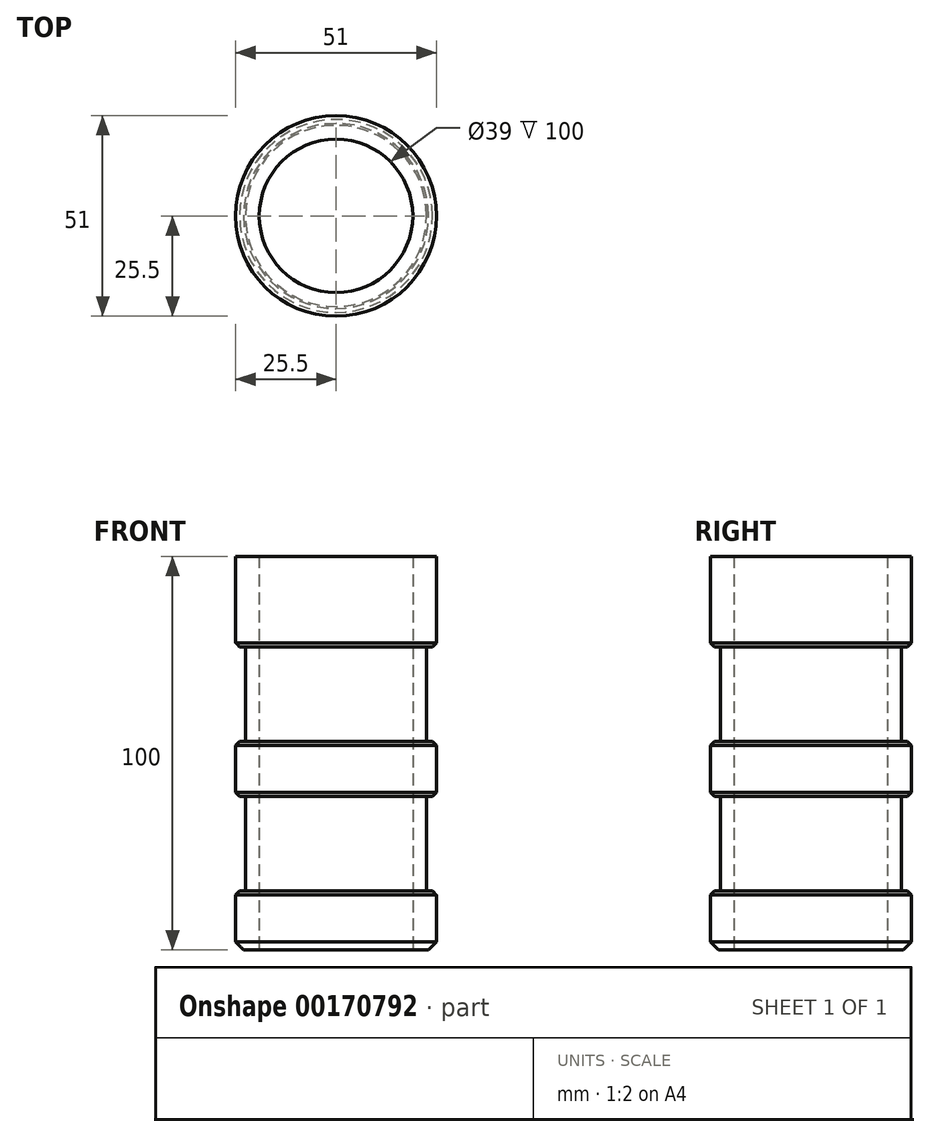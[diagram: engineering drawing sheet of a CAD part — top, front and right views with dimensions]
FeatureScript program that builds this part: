
annotation { "Feature Type Name" : "Feature", "Feature Type Description" : "" }
export const myFeature = defineFeature(function(context is Context, id is Id, definition is map)
    precondition{}
    {
        {
            var Q0;
            Q0=qCreatedBy(makeId("Front.planeOp"),FACE);
            var sketch = newSketch(context, id + "F0", { "sketchPlane" : qUnion([Q0])});
            skLineSegment(sketch, "E0", {"start": v(0, 0) * mm, "end": v(0, 234.52) * mm, "construction": true});
            skLineSegment(sketch, "E1", {"start": v(19.5, 0) * mm, "end": v(23.5, 0) * mm});
            skLineSegment(sketch, "E2", {"start": v(23.5, 0) * mm, "end": v(25.5, 2) * mm});
            skLineSegment(sketch, "E3", {"start": v(25.5, 2) * mm, "end": v(25.5, 15) * mm});
            skLineSegment(sketch, "E4", {"start": v(25.5, 15) * mm, "end": v(23, 15) * mm});
            skLineSegment(sketch, "E5", {"start": v(23, 15) * mm, "end": v(23, 39) * mm});
            skLineSegment(sketch, "E6", {"start": v(23, 39) * mm, "end": v(25.5, 39) * mm});
            skLineSegment(sketch, "E7", {"start": v(25.5, 39) * mm, "end": v(25.5, 53) * mm});
            skLineSegment(sketch, "E8", {"start": v(25.5, 53) * mm, "end": v(23, 53) * mm});
            skLineSegment(sketch, "E9", {"start": v(23, 53) * mm, "end": v(23, 77) * mm});
            skLineSegment(sketch, "E10", {"start": v(23, 77) * mm, "end": v(25.5, 77) * mm});
            skLineSegment(sketch, "E11", {"start": v(25.5, 77) * mm, "end": v(25.5, 100) * mm});
            skLineSegment(sketch, "E12", {"start": v(25.5, 100) * mm, "end": v(19.5, 100) * mm});
            skLineSegment(sketch, "E13", {"start": v(25.5, 100) * mm, "end": v(32.92, 100) * mm});
            skLineSegment(sketch, "E14", {"start": v(19.5, 100) * mm, "end": v(19.5, 0) * mm});
            skPoint(sketch, "E15.start.orphan", {"position": v(0, 100) * mm});
            skSolve(sketch);
        }
        {
            var Q0;
            Q0=makeQuery(id+"F0.imprint","IMPRINT",FACE,{"disambiguationData":[TD([[makeQuery(id+"F0.imprint","IMPRINT",EDGE,{"derivedFrom":sQuery(id+"F0.wireOp",EDGE,"E1")}),1.0]])]});
            var Q1;
            Q1=sQuery(id+"F0.wireOp",EDGE,"E0");
            revolve(context, id + "F1", {"entities" : qUnion([Q0]), "axis" : qUnion([Q1]), "revolveType" : RevolveType.FULL});
        }
        {
            var Q0;
            Q0=makeQuery(id+"F1.opRevolve","SWEPT_EDGE",EDGE,{"disambiguationData":[OSD([sQuery(id+"F0.wireOp",EDGE,"E10"),sQuery(id+"F0.wireOp",EDGE,"E11")])]});
            var Q1;
            Q1=makeQuery(id+"F1.opRevolve","SWEPT_EDGE",EDGE,{"disambiguationData":[OSD([sQuery(id+"F0.wireOp",EDGE,"E7"),sQuery(id+"F0.wireOp",EDGE,"E8")])]});
            var Q2;
            Q2=makeQuery(id+"F1.opRevolve","SWEPT_EDGE",EDGE,{"disambiguationData":[OSD([sQuery(id+"F0.wireOp",EDGE,"E6"),sQuery(id+"F0.wireOp",EDGE,"E7")])]});
            var Q3;
            Q3=makeQuery(id+"F1.opRevolve","SWEPT_EDGE",EDGE,{"disambiguationData":[OSD([sQuery(id+"F0.wireOp",EDGE,"E3"),sQuery(id+"F0.wireOp",EDGE,"E4")])]});
            chamfer(context, id + "F2", {"entities" : qUnion([Q0, Q1, Q2, Q3]), "width" : 1 * mm, "tangentPropagation" : true});
        }
    });
